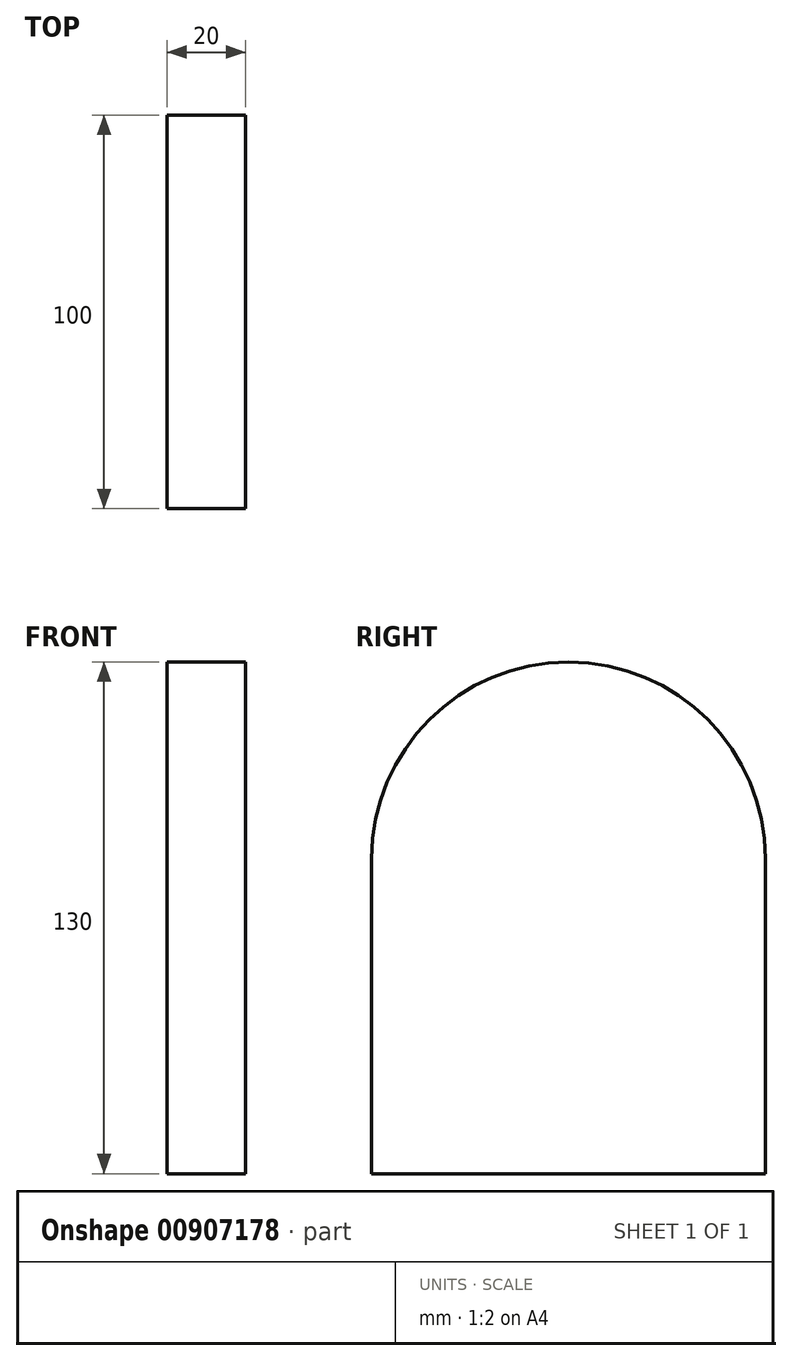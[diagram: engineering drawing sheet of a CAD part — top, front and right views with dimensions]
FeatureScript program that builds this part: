
annotation { "Feature Type Name" : "Feature", "Feature Type Description" : "" }
export const myFeature = defineFeature(function(context is Context, id is Id, definition is map)
    precondition{}
    {
        {
            var Q0;
            Q0=qCreatedBy(makeId("Right.planeOp"),FACE);
            var sketch = newSketch(context, id + "F0", { "sketchPlane" : qUnion([Q0])});
            skArc(sketch, "E0", {"start": v(50, 0) * mm, "mid": v(0, 50) * mm, "end": v(-50, 0) * mm});
            skLineSegment(sketch, "E1", {"start": v(-50, 0) * mm, "end": v(-50, -80) * mm});
            skLineSegment(sketch, "E2", {"start": v(-50, -80) * mm, "end": v(0, -80) * mm});
            skLineSegment(sketch, "E3", {"start": v(50, 0) * mm, "end": v(50, -80) * mm});
            skLineSegment(sketch, "E4", {"start": v(50, -80) * mm, "end": v(0, -80) * mm});
            skSolve(sketch);
        }
        {
            var Q0;
            Q0=makeQuery(id+"F0.imprint","IMPRINT",FACE,{"disambiguationData":[TD([[makeQuery(id+"F0.imprint","IMPRINT",EDGE,{"derivedFrom":sQuery(id+"F0.wireOp",EDGE,"E0")}),1.0]])]});
            extrude(context, id + "F1", {"entities" : qUnion([Q0]), "depth" : 20 * mm, "offsetDistance" : 25 * mm});
        }
    });
